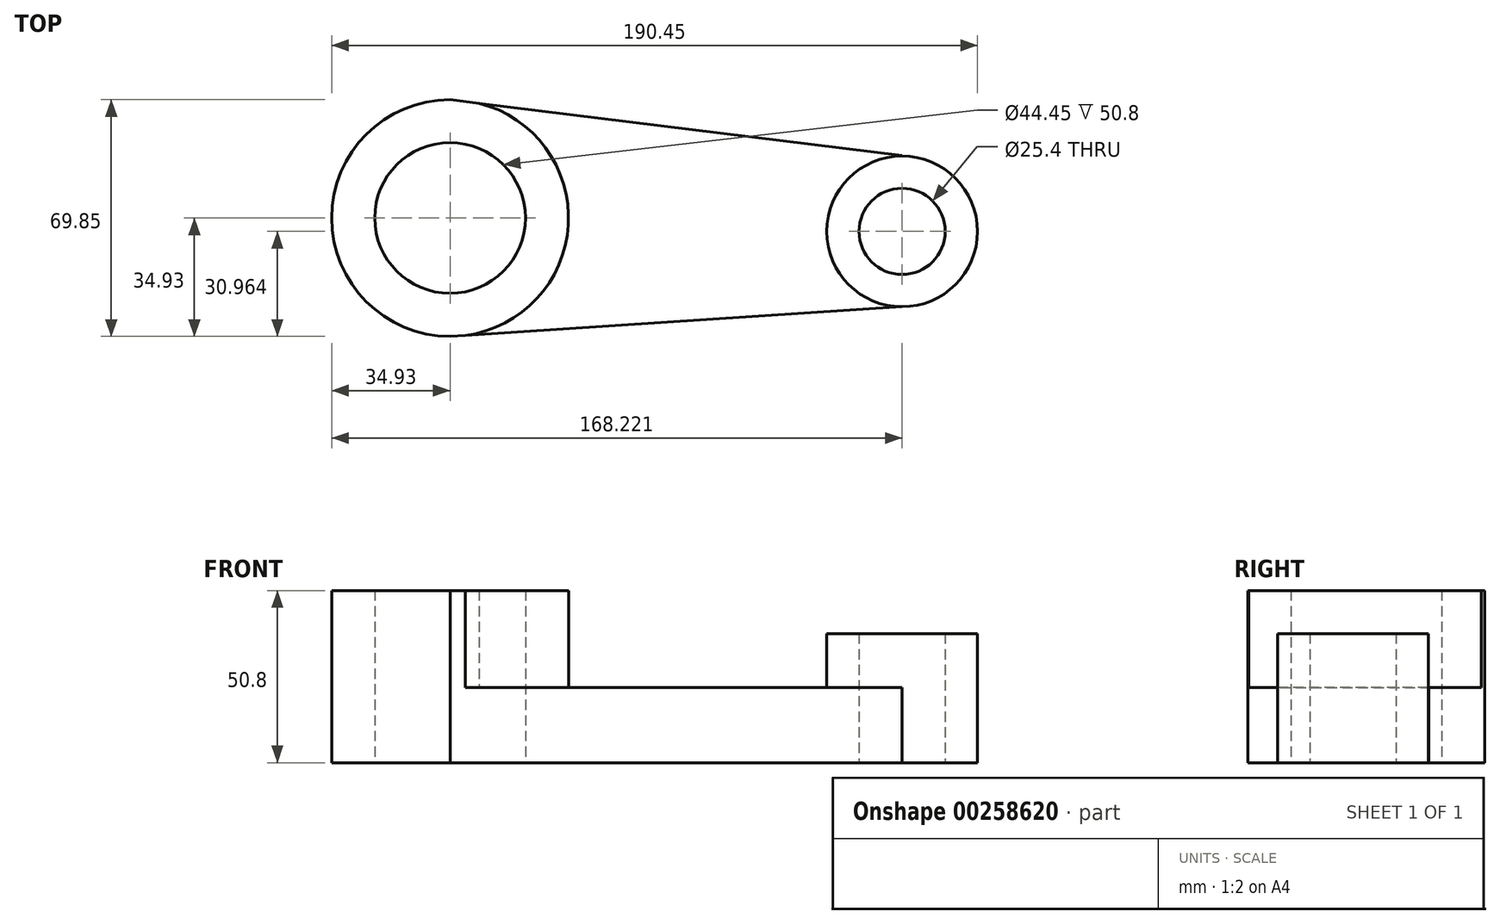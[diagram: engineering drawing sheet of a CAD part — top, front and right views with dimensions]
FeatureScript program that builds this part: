
annotation { "Feature Type Name" : "Feature", "Feature Type Description" : "" }
export const myFeature = defineFeature(function(context is Context, id is Id, definition is map)
    precondition{}
    {
        {
            var Q0;
            Q0=qCreatedBy(makeId("Top.planeOp"),FACE);
            var sketch = newSketch(context, id + "F0", { "sketchPlane" : qUnion([Q0])});
            skCircle(sketch, "E0", {"center": v(0, 0) * mm, "radius": 34.93 * mm});
            skCircle(sketch, "E1", {"center": v(133.3, -3.97) * mm, "radius": 22.23 * mm});
            skLineSegment(sketch, "E2", {"start": v(133.3, -26.2) * mm, "end": v(0, -34.93) * mm});
            skLineSegment(sketch, "E3", {"start": v(0, 0) * mm, "end": v(133.3, -3.97) * mm});
            skLineSegment(sketch, "E4", {"start": v(0, 34.92) * mm, "end": v(133.3, 18.43) * mm});
            skLineSegment(sketch, "E5", {"start": v(133.3, 18.43) * mm, "end": v(133.3, 18.26) * mm});
            skCircle(sketch, "E6", {"center": v(0, 0) * mm, "radius": 22.23 * mm});
            skCircle(sketch, "E7", {"center": v(133.3, -3.97) * mm, "radius": 12.7 * mm});
            skLineSegment(sketch, "E8", {"start": v(0, 0) * mm, "end": v(-1.04, -34.93) * mm});
            skSolve(sketch);
        }
        {
            var Q0;
            Q0=makeQuery(id+"F0.imprint","IMPRINT",FACE,{"disambiguationData":[TD([[makeQuery(id+"F0.imprint","IMPRINT",EDGE,{"derivedFrom":sQuery(id+"F0.wireOp",EDGE,"E6")}),-1.0]])]});
            var Q1;
            {var subQ0=sQuery(id+"F0.wireOp",EDGE,"E2");var subQ1=sQuery(id+"F0.wireOp",EDGE,"E0");var subQ2=makeQuery(id+"F0.imprint","INTERSECT",VERTEX,{"disambiguationData":[OD(1.0)],"derivedFrom":[subQ1,subQ0]});Q1=makeQuery(id+"F0.imprint","IMPRINT",FACE,{"disambiguationData":[TD([[makeQuery(id+"F0.imprint","IMPRINT",EDGE,{"disambiguationData":[TD([[subQ2,-1.0]])],"derivedFrom":subQ1}),-1.0]])]});}
            var Q2;
            {var subQ0=sQuery(id+"F0.wireOp",EDGE,"E5");Q2=makeQuery(id+"F0.imprint","IMPRINT",FACE,{"disambiguationData":[TD([[makeQuery(id+"F0.imprint","IMPRINT",EDGE,{"derivedFrom":subQ0}),-1.0]])]});}
            var Q3;
            Q3=makeQuery(id+"F0.imprint","IMPRINT",FACE,{"disambiguationData":[TD([[makeQuery(id+"F0.imprint","IMPRINT",EDGE,{"derivedFrom":sQuery(id+"F0.wireOp",EDGE,"E7")}),-1.0]])]});
            extrude(context, id + "F1", {"entities" : qUnion([Q0, Q1, Q2, Q3]), "depth" : 22.22 * mm});
        }
        {
            var Q0;
            Q0=makeQuery(id+"F0.imprint","IMPRINT",FACE,{"disambiguationData":[TD([[makeQuery(id+"F0.imprint","IMPRINT",EDGE,{"derivedFrom":sQuery(id+"F0.wireOp",EDGE,"E6")}),-1.0]])]});
            extrude(context, id + "F2", {"entities" : qUnion([Q0]), "operationType" : NewBodyOperationType.ADD, "depth" : 50.8 * mm});
        }
        {
            var Q0;
            Q0=makeQuery(id+"F0.imprint","IMPRINT",FACE,{"disambiguationData":[TD([[makeQuery(id+"F0.imprint","IMPRINT",EDGE,{"derivedFrom":sQuery(id+"F0.wireOp",EDGE,"E7")}),-1.0]])]});
            extrude(context, id + "F3", {"entities" : qUnion([Q0]), "operationType" : NewBodyOperationType.ADD, "depth" : 38.1 * mm});
        }
    });
